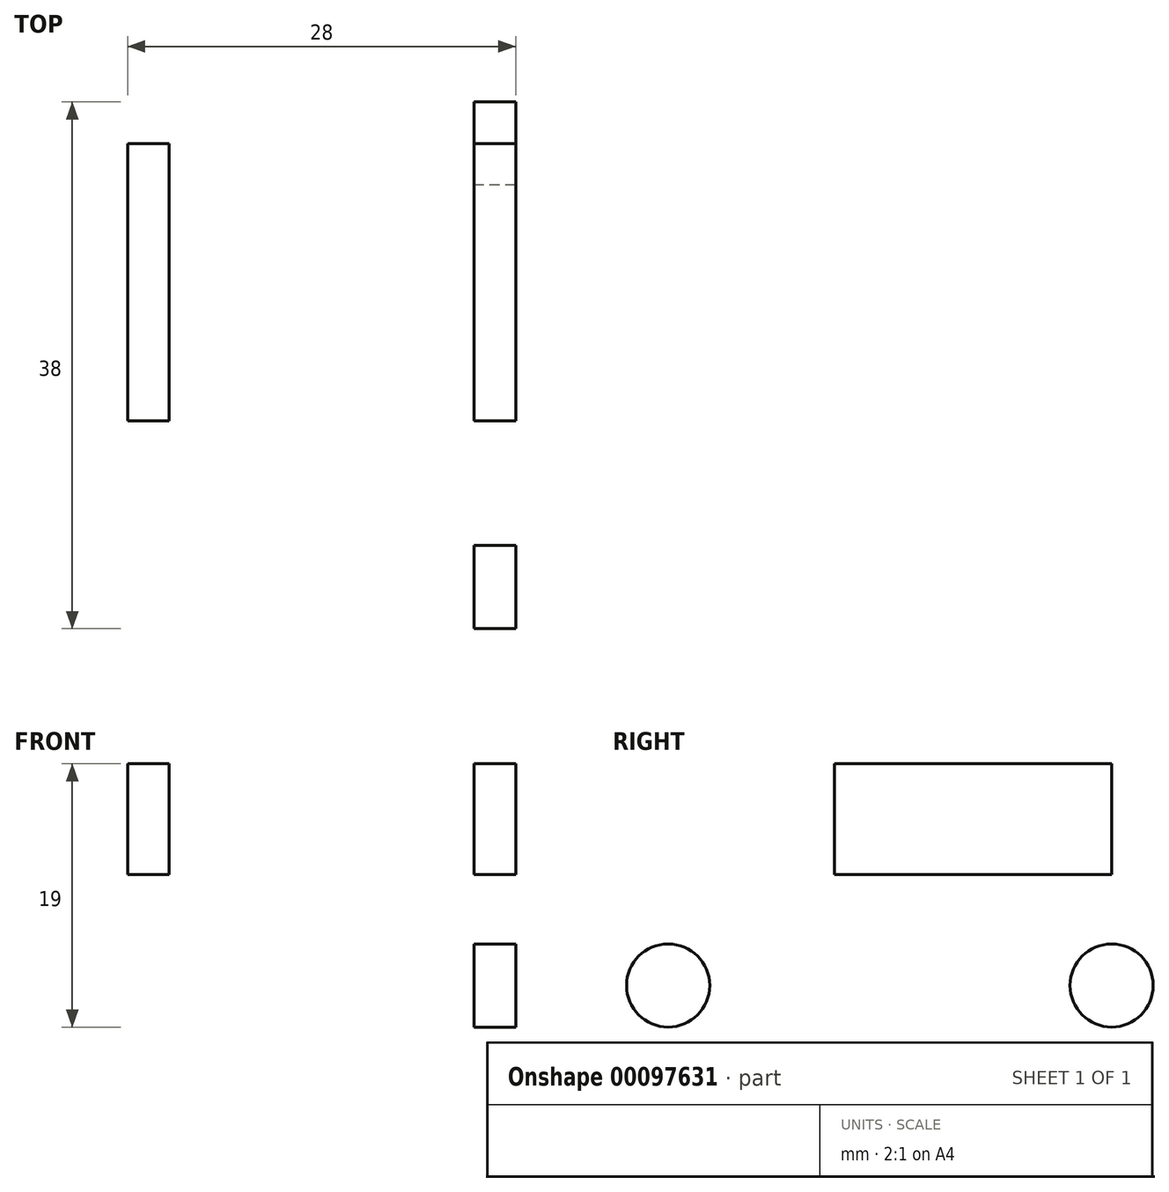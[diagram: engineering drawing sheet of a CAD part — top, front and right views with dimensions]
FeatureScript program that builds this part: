
annotation { "Feature Type Name" : "Feature", "Feature Type Description" : "" }
export const myFeature = defineFeature(function(context is Context, id is Id, definition is map)
    precondition{}
    {
        {
            var Q0;
            Q0=qCreatedBy(makeId("Right.planeOp"),FACE);
            var sketch = newSketch(context, id + "F0", { "sketchPlane" : qUnion([Q0])});
            skLineSegment(sketch, "E0", {"start": v(-18.38, 9.09) * mm, "end": v(13.62, 9.09) * mm, "construction": true});
            skArc(sketch, "E1.0.startCap", {"start": v(-18.38, 1.09) * mm, "mid": v(-26.38, 9.09) * mm, "end": v(-18.38, 17.09) * mm});
            skArc(sketch, "E1.0.endCap", {"start": v(13.62, 17.09) * mm, "mid": v(21.62, 9.09) * mm, "end": v(13.62, 1.09) * mm});
            skLineSegment(sketch, "E1.0.left", {"start": v(-18.38, 17.09) * mm, "end": v(13.62, 17.09) * mm});
            skLineSegment(sketch, "E1.0.right", {"start": v(-18.38, 1.09) * mm, "end": v(13.62, 1.09) * mm});
            skLineSegment(sketch, "E2", {"start": v(13.62, 17.09) * mm, "end": v(13.62, 25.09) * mm});
            skLineSegment(sketch, "E3", {"start": v(13.62, 25.09) * mm, "end": v(-6.38, 25.09) * mm});
            skLineSegment(sketch, "E4", {"start": v(-6.38, 25.09) * mm, "end": v(-6.38, 17.09) * mm});
            skCircle(sketch, "E5", {"center": v(-18.38, 9.09) * mm, "radius": 3 * mm});
            skCircle(sketch, "E6", {"center": v(13.62, 9.09) * mm, "radius": 3 * mm});
            skSolve(sketch);
        }
        {
            var Q0;
            {var subQ3=sQuery(id+"F0.wireOp",EDGE,"E1.0.startCap");Q0=makeQuery(id+"F0.imprint","IMPRINT",FACE,{"disambiguationData":[TD([[makeQuery(id+"F0.imprint","IMPRINT",EDGE,{"derivedFrom":subQ3}),-1.0]])]});}
            var Q1;
            {var subQ0=sQuery(id+"F0.wireOp",EDGE,"E2");Q1=makeQuery(id+"F0.imprint","IMPRINT",FACE,{"disambiguationData":[TD([[makeQuery(id+"F0.imprint","IMPRINT",EDGE,{"derivedFrom":subQ0}),1.0]])]});}
            var Q2;
            Q2=makeQuery(id+"F0.imprint","IMPRINT",FACE,{"disambiguationData":[TD([[makeQuery(id+"F0.imprint","IMPRINT",EDGE,{"derivedFrom":sQuery(id+"F0.wireOp",EDGE,"E5")}),1.0]])]});
            var Q3;
            Q3=makeQuery(id+"F0.imprint","IMPRINT",FACE,{"disambiguationData":[TD([[makeQuery(id+"F0.imprint","IMPRINT",EDGE,{"derivedFrom":sQuery(id+"F0.wireOp",EDGE,"E6")}),1.0]])]});
            extrude(context, id + "F1", {"entities" : qUnion([Q0, Q1, Q2, Q3]), "depth" : 3 * mm});
        }
        {
            var Q0;
            Q0=makeQuery(id+"F1.opExtrude","SWEPT_FACE",FACE,{"disambiguationData":[OSD([sQuery(id+"F0.wireOp",EDGE,"E3")])]});
            var sketch = newSketch(context, id + "F2", { "sketchPlane" : qUnion([Q0])});
            skLineSegment(sketch, "E7", {"start": v(3, 13.62) * mm, "end": v(-11, 13.62) * mm});
            skLineSegment(sketch, "E8", {"start": v(3, -6.38) * mm, "end": v(-11, -6.38) * mm});
            skLineSegment(sketch, "E9", {"start": v(-11, 13.62) * mm, "end": v(-11, -6.38) * mm});
            skSolve(sketch);
        }
        {
            var Q0;
            Q0=sQuery(id+"F2.wireOp",EDGE,"E8");
            var Q1;
            Q1=sQuery(id+"F2.wireOp",EDGE,"E9");
            var Q2;
            Q2=sQuery(id+"F2.wireOp",EDGE,"E7");
            extrude(context, id + "F3", {"bodyType" : ToolBodyType.SURFACE, "surfaceEntities" : qUnion([Q0, Q1, Q2]), "oppositeDirection" : true, "depth" : 3 * mm});
        }
        {
            var Q0;
            Q0=makeQuery(id+"F1.opExtrude","SWEPT_BODY",BODY,{"disambiguationData":[OSD([sQuery(id+"F0.wireOp",EDGE,"E1.0.startCap"),sQuery(id+"F0.wireOp",EDGE,"E1.0.endCap"),sQuery(id+"F0.wireOp",EDGE,"E1.0.left"),sQuery(id+"F0.wireOp",EDGE,"E1.0.right"),sQuery(id+"F0.wireOp",EDGE,"E2"),sQuery(id+"F0.wireOp",EDGE,"E3"),sQuery(id+"F0.wireOp",EDGE,"E4")])]});
            var Q1;
            Q1=makeQuery(id+"F3.opExtrude","SWEPT_BODY",BODY,{"disambiguationData":[OSD([sQuery(id+"F2.wireOp",EDGE,"E7")])]});
            var Q2;
            Q2=makeQuery(id+"F3.opExtrude","SWEPT_FACE",FACE,{"disambiguationData":[OSD([sQuery(id+"F2.wireOp",EDGE,"E9")])]});
            mirror(context, id + "F4", {"entities" : qUnion([Q0, Q1]), "mirrorPlane" : qUnion([Q2])});
        }
    });
